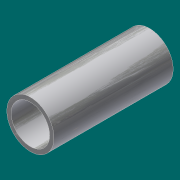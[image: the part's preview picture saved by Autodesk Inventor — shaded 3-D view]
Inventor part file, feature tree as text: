
AUTODESK INVENTOR PART (.ipt)
format: ipt  version: 2017 (Build 210142000, 142)  size: 90,624 bytes
history: native  units: in
note: dims shown in document units (in); Inventor stores cm internally (conversion verified against a paired STEP export)
features: extrude x1, sketch x1
ambient origin geometry x8: Origin, YZ Plane, XZ Plane, XY Plane, X Axis, Y Axis, Z Axis, Center Point
bodies: Solid1 (feature_tree)
feature tree (2):
  extrude  "Extrusion1"  Depth=6.0in
  sketch  "Sketch1"  dims[d0=2.375in d1=1.939in d2=6.0in d3=0.0in]
